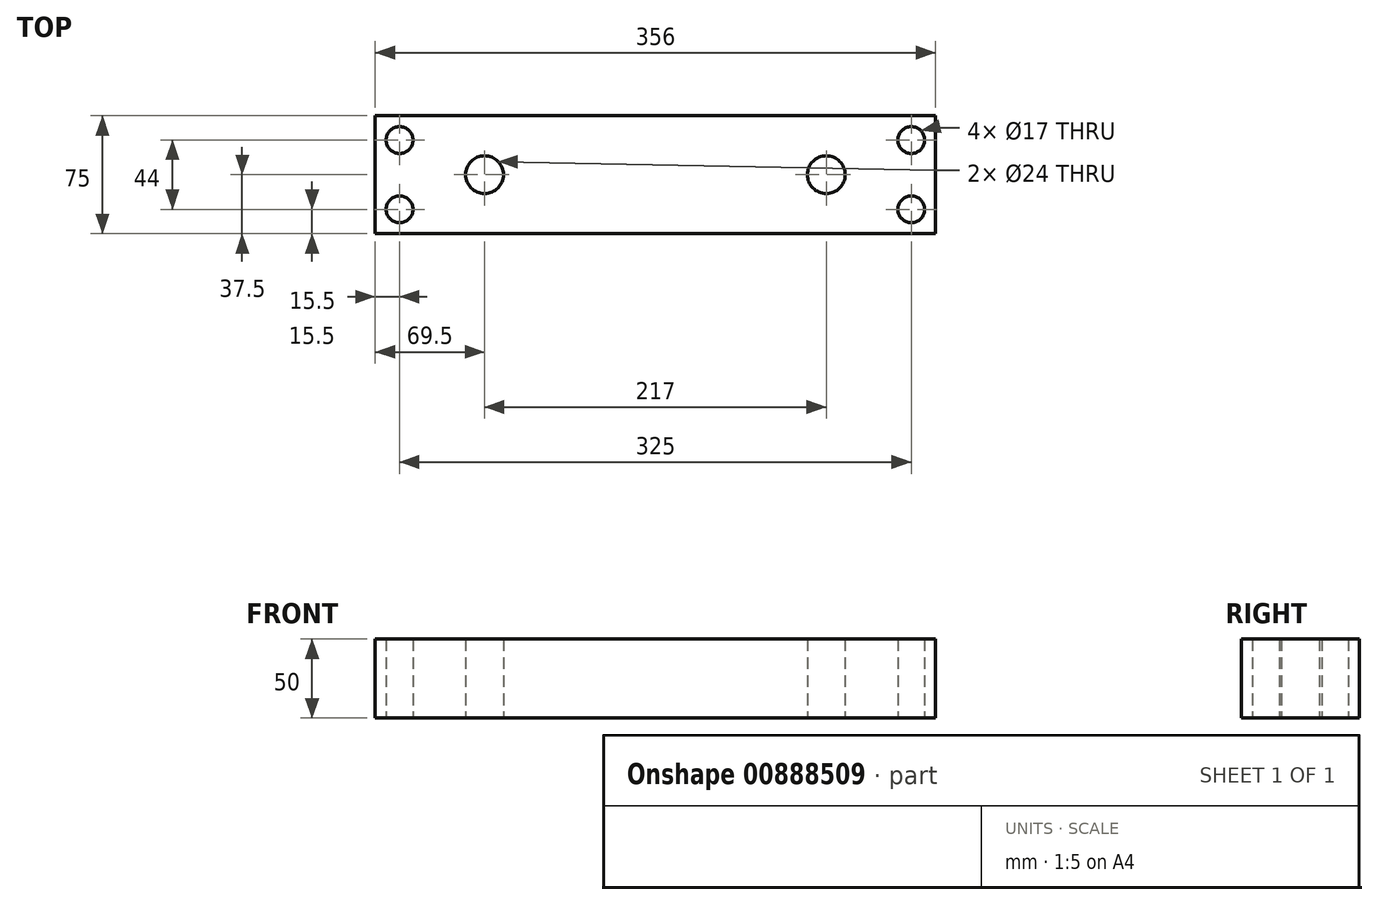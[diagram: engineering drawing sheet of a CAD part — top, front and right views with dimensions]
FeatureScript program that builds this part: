
annotation { "Feature Type Name" : "Feature", "Feature Type Description" : "" }
export const myFeature = defineFeature(function(context is Context, id is Id, definition is map)
    precondition{}
    {
        {
            var Q0;
            Q0=qCreatedBy(makeId("Top.planeOp"),FACE);
            var sketch = newSketch(context, id + "F0", { "sketchPlane" : qUnion([Q0])});
            skLineSegment(sketch, "E0.bottom", {"start": v(-178, 37.5) * mm, "end": v(178, 37.5) * mm});
            skLineSegment(sketch, "E0.top", {"start": v(-178, -37.5) * mm, "end": v(178, -37.5) * mm});
            skLineSegment(sketch, "E0.left", {"start": v(-178, 37.5) * mm, "end": v(-178, -37.5) * mm});
            skLineSegment(sketch, "E0.right", {"start": v(178, 37.5) * mm, "end": v(178, -37.5) * mm});
            skPoint(sketch, "E0.middle", {"position": v(0, 0) * mm});
            skLineSegment(sketch, "E1", {"start": v(0, 0) * mm, "end": v(0, 22) * mm, "construction": true});
            skLineSegment(sketch, "E2", {"start": v(0, 22) * mm, "end": v(-162.5, 22) * mm, "construction": true});
            skLineSegment(sketch, "E3", {"start": v(0, 22) * mm, "end": v(162.5, 22) * mm, "construction": true});
            skLineSegment(sketch, "E4", {"start": v(0, 0) * mm, "end": v(0, -22) * mm, "construction": true});
            skLineSegment(sketch, "E5", {"start": v(0, -22) * mm, "end": v(162.5, -22) * mm, "construction": true});
            skLineSegment(sketch, "E6", {"start": v(0, -22) * mm, "end": v(-162.5, -22) * mm, "construction": true});
            skCircle(sketch, "E7", {"center": v(-162.5, 22) * mm, "radius": 8.5 * mm});
            skCircle(sketch, "E8", {"center": v(162.5, 22) * mm, "radius": 8.5 * mm});
            skCircle(sketch, "E9", {"center": v(162.5, -22) * mm, "radius": 8.5 * mm});
            skCircle(sketch, "E10", {"center": v(-162.5, -22) * mm, "radius": 8.5 * mm});
            skLineSegment(sketch, "E11", {"start": v(0, 0) * mm, "end": v(108.5, 0) * mm, "construction": true});
            skLineSegment(sketch, "E12", {"start": v(0, 0) * mm, "end": v(-108.5, 0) * mm, "construction": true});
            skCircle(sketch, "E13", {"center": v(108.5, 0) * mm, "radius": 13 * mm});
            skCircle(sketch, "E14", {"center": v(-108.5, 0) * mm, "radius": 13 * mm});
            skCircle(sketch, "E15", {"center": v(108.5, 0) * mm, "radius": 18 * mm});
            skCircle(sketch, "E16", {"center": v(162.5, -22) * mm, "radius": 12 * mm});
            skLineSegment(sketch, "E17", {"start": v(0, 11) * mm, "end": v(-137.5, 11) * mm, "construction": true});
            skLineSegment(sketch, "E18", {"start": v(0, 11) * mm, "end": v(137.5, 11) * mm, "construction": true});
            skSolve(sketch);
        }
        {
            var Q0;
            Q0 = qSketchRegion(id + "F0", true);
            var Q1;
            Q1=makeQuery(id+"F0.imprint","IMPRINT",FACE,{"disambiguationData":[TD([[makeQuery(id+"F0.imprint","IMPRINT",EDGE,{"derivedFrom":sQuery(id+"F0.wireOp",EDGE,"E9")}),-1.0]])]});
            var Q2;
            Q2=makeQuery(id+"F0.imprint","IMPRINT",FACE,{"disambiguationData":[TD([[makeQuery(id+"F0.imprint","IMPRINT",EDGE,{"derivedFrom":sQuery(id+"F0.wireOp",EDGE,"E13")}),-1.0]])]});
            var Q3;
            Q3=makeQuery(id+"F0.imprint","IMPRINT",FACE,{"disambiguationData":[TD([[makeQuery(id+"F0.imprint","IMPRINT",EDGE,{"derivedFrom":sQuery(id+"F0.wireOp",EDGE,"E14")}),1.0]])]});
            var Q4;
            Q4=makeQuery(id+"F0.imprint","IMPRINT",FACE,{"disambiguationData":[TD([[makeQuery(id+"F0.imprint","IMPRINT",EDGE,{"derivedFrom":sQuery(id+"F0.wireOp",EDGE,"E13")}),1.0]])]});
            extrude(context, id + "F1", {"entities" : qUnion([Q0, Q1, Q2, Q3, Q4]), "depth" : 50 * mm, "offsetDistance" : 25 * mm});
        }
        {
            var Q0;
            Q0=sQuery(id+"F0.wireOp",VERTEX,"E12.end");
            var Q1;
            Q1=sQuery(id+"F0.wireOp",VERTEX,"E11.end");
            var Q2;
            Q2=makeQuery(id+"F1.opExtrude","SWEPT_BODY",BODY,{"disambiguationData":[OSD([sQuery(id+"F0.wireOp",EDGE,"E0.bottom"),sQuery(id+"F0.wireOp",EDGE,"E0.top"),sQuery(id+"F0.wireOp",EDGE,"E0.left"),sQuery(id+"F0.wireOp",EDGE,"E0.right"),sQuery(id+"F0.wireOp",EDGE,"E7"),sQuery(id+"F0.wireOp",EDGE,"E8"),sQuery(id+"F0.wireOp",EDGE,"E9"),sQuery(id+"F0.wireOp",EDGE,"E10")])]});
            hole(context, id + "F2", {"style" : HoleStyle.SIMPLE, "endStyle" : HoleEndStyle.THROUGH, "oppositeDirection" : true, "holeDiameter" : 24 * mm, "majorDiameter" : 20 * mm, "isTappedThrough" : true, "tappedDepth" : 12 * mm, "tapClearance" : 3, "startFromSketch" : true, "locations" : qUnion([Q0, Q1]), "scope" : qUnion([Q2])});
        }
    });
